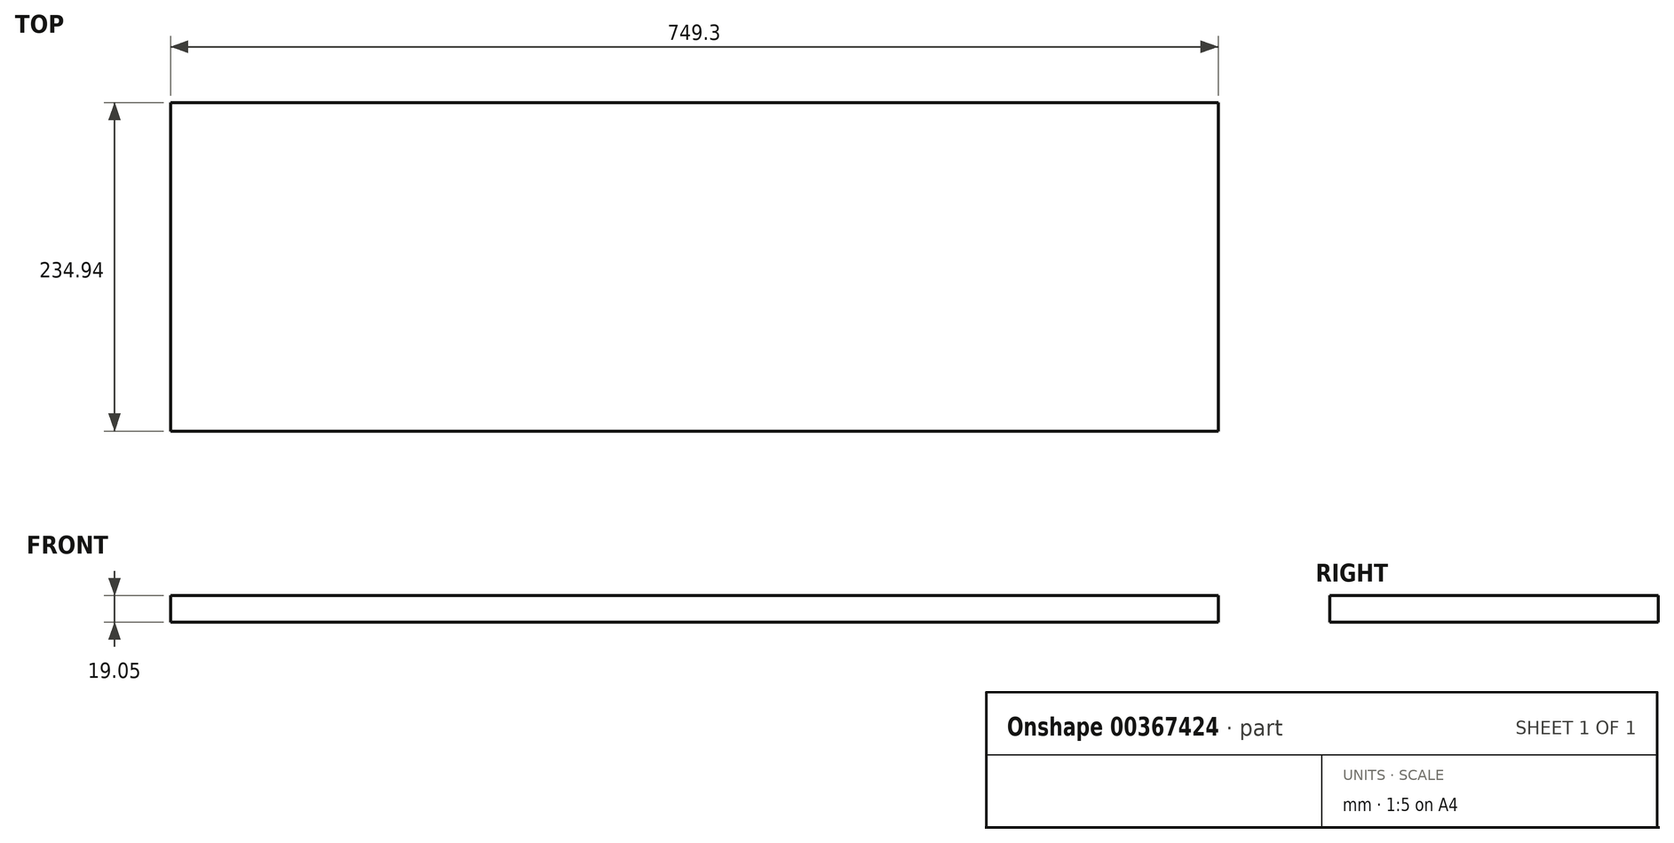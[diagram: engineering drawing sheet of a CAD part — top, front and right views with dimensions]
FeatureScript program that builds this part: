
annotation { "Feature Type Name" : "Feature", "Feature Type Description" : "" }
export const myFeature = defineFeature(function(context is Context, id is Id, definition is map)
    precondition{}
    {
        {
            var Q0;
            Q0=qCreatedBy(makeId("Top.planeOp"),FACE);
            var sketch = newSketch(context, id + "F0", { "sketchPlane" : qUnion([Q0])});
            skLineSegment(sketch, "E0.bottom", {"start": v(374.65, 117.48) * mm, "end": v(-374.65, 117.48) * mm});
            skLineSegment(sketch, "E0.top", {"start": v(374.65, -117.48) * mm, "end": v(-374.65, -117.48) * mm});
            skLineSegment(sketch, "E0.left", {"start": v(374.65, 117.48) * mm, "end": v(374.65, -117.48) * mm});
            skLineSegment(sketch, "E0.right", {"start": v(-374.65, 117.48) * mm, "end": v(-374.65, -117.48) * mm});
            skPoint(sketch, "E0.middle", {"position": v(0, 0) * mm});
            skSolve(sketch);
        }
        {
            var Q0;
            Q0 = qSketchRegion(id + "F0", true);
            extrude(context, id + "F1", {"entities" : qUnion([Q0]), "depth" : 19.05 * mm});
        }
    });
